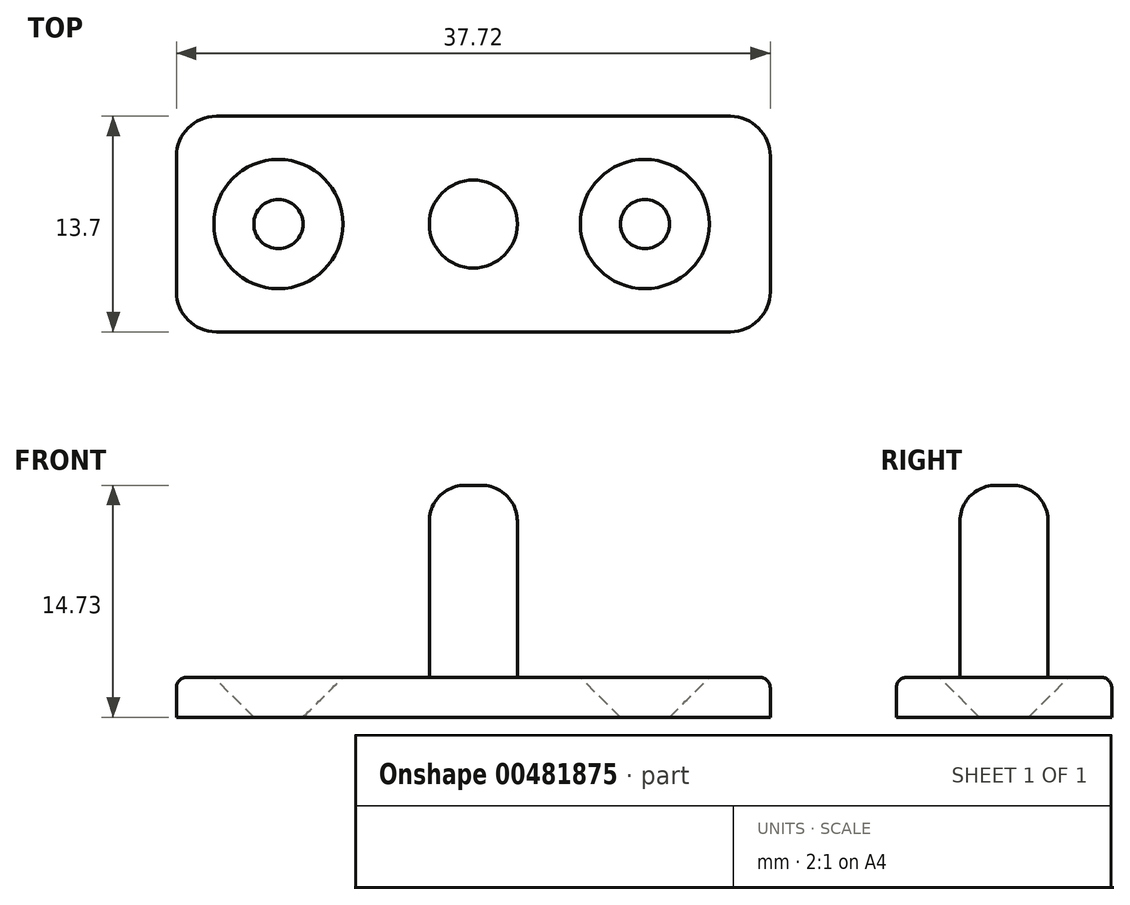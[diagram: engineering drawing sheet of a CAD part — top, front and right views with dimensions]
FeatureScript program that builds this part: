
annotation { "Feature Type Name" : "Feature", "Feature Type Description" : "" }
export const myFeature = defineFeature(function(context is Context, id is Id, definition is map)
    precondition{}
    {
        {
            var Q0;
            Q0=qCreatedBy(makeId("Top.planeOp"),FACE);
            var sketch = newSketch(context, id + "F0", { "sketchPlane" : qUnion([Q0])});
            skLineSegment(sketch, "E0.bottom", {"start": v(18.86, -6.85) * mm, "end": v(-18.86, -6.85) * mm});
            skLineSegment(sketch, "E0.top", {"start": v(18.86, 6.85) * mm, "end": v(-18.86, 6.85) * mm});
            skLineSegment(sketch, "E0.left", {"start": v(18.86, -6.85) * mm, "end": v(18.86, 6.85) * mm});
            skLineSegment(sketch, "E0.right", {"start": v(-18.86, -6.85) * mm, "end": v(-18.86, 6.85) * mm});
            skPoint(sketch, "E0.middle", {"position": v(0, 0) * mm});
            skCircle(sketch, "E1", {"center": v(-12.38, 0) * mm, "radius": 1.56 * mm});
            skCircle(sketch, "E2", {"center": v(10.9, 0) * mm, "radius": 1.56 * mm});
            skCircle(sketch, "E3", {"center": v(0, 0) * mm, "radius": 2.8 * mm});
            skSolve(sketch);
        }
        {
            var Q0;
            Q0=makeQuery(id+"F0.imprint","IMPRINT",FACE,{"disambiguationData":[TD([[makeQuery(id+"F0.imprint","IMPRINT",EDGE,{"derivedFrom":sQuery(id+"F0.wireOp",EDGE,"E3")}),1.0]])]});
            extrude(context, id + "F1", {"entities" : qUnion([Q0]), "depth" : 14.73 * mm});
        }
        {
            var Q0;
            Q0=makeQuery(id+"F0.imprint","IMPRINT",FACE,{"disambiguationData":[TD([[makeQuery(id+"F0.imprint","IMPRINT",EDGE,{"derivedFrom":sQuery(id+"F0.wireOp",EDGE,"E0.bottom")}),-1.0]])]});
            extrude(context, id + "F2", {"entities" : qUnion([Q0]), "operationType" : NewBodyOperationType.ADD, "depth" : 2.54 * mm});
        }
        {
            var Q0;
            Q0=makeQuery(id+"F2.opExtrude","CAP_EDGE",EDGE,{"disambiguationData":[OSD([sQuery(id+"F0.wireOp",EDGE,"E1")])],"isStart":false});
            var Q1;
            Q1=makeQuery(id+"F2.opExtrude","CAP_EDGE",EDGE,{"disambiguationData":[OSD([sQuery(id+"F0.wireOp",EDGE,"E2")])],"isStart":false});
            chamfer(context, id + "F3", {"entities" : qUnion([Q0, Q1]), "width" : 2.54 * mm, "tangentPropagation" : true});
        }
        {
            var Q0;
            Q0=makeQuery(id+"F2.opExtrude","SWEPT_EDGE",EDGE,{"disambiguationData":[OSD([sQuery(id+"F0.wireOp",EDGE,"E0.bottom"),sQuery(id+"F0.wireOp",EDGE,"E0.left")])]});
            var Q1;
            Q1=makeQuery(id+"F2.opExtrude","SWEPT_EDGE",EDGE,{"disambiguationData":[OSD([sQuery(id+"F0.wireOp",EDGE,"E0.top"),sQuery(id+"F0.wireOp",EDGE,"E0.left")])]});
            var Q2;
            Q2=makeQuery(id+"F2.opExtrude","SWEPT_EDGE",EDGE,{"disambiguationData":[OSD([sQuery(id+"F0.wireOp",EDGE,"E0.bottom"),sQuery(id+"F0.wireOp",EDGE,"E0.right")])]});
            var Q3;
            Q3=makeQuery(id+"F2.opExtrude","SWEPT_EDGE",EDGE,{"disambiguationData":[OSD([sQuery(id+"F0.wireOp",EDGE,"E0.top"),sQuery(id+"F0.wireOp",EDGE,"E0.right")])]});
            fillet(context, id + "F4", {"entities" : qUnion([Q0, Q1, Q2, Q3]), "radius" : 2.54 * mm, "tangentPropagation" : true, "allowEdgeOverflow" : false});
        }
        {
            var Q0;
            Q0=makeQuery(id+"F1.opExtrude","CAP_EDGE",EDGE,{"disambiguationData":[OSD([sQuery(id+"F0.wireOp",EDGE,"E3")])],"isStart":false});
            fillet(context, id + "F5", {"entities" : qUnion([Q0]), "radius" : 2.27 * mm, "tangentPropagation" : true, "allowEdgeOverflow" : false});
        }
        {
            var Q0;
            Q0=makeQuery(id+"F2.opExtrude","CAP_EDGE",EDGE,{"disambiguationData":[OSD([sQuery(id+"F0.wireOp",EDGE,"E0.bottom")])],"isStart":false});
            var Q1;
            {var subQ0=sQuery(id+"F0.wireOp",EDGE,"E0.left");var subQ1=sQuery(id+"F0.wireOp",EDGE,"E0.bottom");Q1=makeQuery(id+"F4.opFillet","BLEND_EDGE",EDGE,{"blendedFrom":[makeQuery(id+"F2.opExtrude","SWEPT_EDGE",EDGE,{"disambiguationData":[OSD([subQ1,subQ0])]}),makeQuery(id+"F2.opExtrude","CAP_FACE",FACE,{"disambiguationData":[OSD([subQ1,sQuery(id+"F0.wireOp",EDGE,"E0.top"),subQ0,sQuery(id+"F0.wireOp",EDGE,"E0.right"),sQuery(id+"F0.wireOp",EDGE,"E1"),sQuery(id+"F0.wireOp",EDGE,"E2"),sQuery(id+"F0.wireOp",EDGE,"E3")])],"isStart":false})],"blendedInto":[makeQuery(id+"F2.opExtrude","CAP_FACE",FACE,{"disambiguationData":[OSD([subQ1,sQuery(id+"F0.wireOp",EDGE,"E0.top"),subQ0,sQuery(id+"F0.wireOp",EDGE,"E0.right"),sQuery(id+"F0.wireOp",EDGE,"E1"),sQuery(id+"F0.wireOp",EDGE,"E2"),sQuery(id+"F0.wireOp",EDGE,"E3")])],"isStart":false})]});}
            var Q2;
            Q2=makeQuery(id+"F2.opExtrude","CAP_EDGE",EDGE,{"disambiguationData":[OSD([sQuery(id+"F0.wireOp",EDGE,"E0.left")])],"isStart":false});
            var Q3;
            Q3=makeQuery(id+"F2.opExtrude","CAP_EDGE",EDGE,{"disambiguationData":[OSD([sQuery(id+"F0.wireOp",EDGE,"E0.top")])],"isStart":false});
            var Q4;
            {var subQ0=sQuery(id+"F0.wireOp",EDGE,"E0.left");var subQ1=sQuery(id+"F0.wireOp",EDGE,"E0.top");Q4=makeQuery(id+"F4.opFillet","BLEND_EDGE",EDGE,{"blendedFrom":[makeQuery(id+"F2.opExtrude","SWEPT_EDGE",EDGE,{"disambiguationData":[OSD([subQ1,subQ0])]}),makeQuery(id+"F2.opExtrude","CAP_FACE",FACE,{"disambiguationData":[OSD([sQuery(id+"F0.wireOp",EDGE,"E0.bottom"),subQ1,subQ0,sQuery(id+"F0.wireOp",EDGE,"E0.right"),sQuery(id+"F0.wireOp",EDGE,"E1"),sQuery(id+"F0.wireOp",EDGE,"E2"),sQuery(id+"F0.wireOp",EDGE,"E3")])],"isStart":false})],"blendedInto":[makeQuery(id+"F2.opExtrude","CAP_FACE",FACE,{"disambiguationData":[OSD([sQuery(id+"F0.wireOp",EDGE,"E0.bottom"),subQ1,subQ0,sQuery(id+"F0.wireOp",EDGE,"E0.right"),sQuery(id+"F0.wireOp",EDGE,"E1"),sQuery(id+"F0.wireOp",EDGE,"E2"),sQuery(id+"F0.wireOp",EDGE,"E3")])],"isStart":false})]});}
            var Q5;
            {var subQ0=sQuery(id+"F0.wireOp",EDGE,"E0.right");var subQ1=sQuery(id+"F0.wireOp",EDGE,"E0.top");Q5=makeQuery(id+"F4.opFillet","BLEND_EDGE",EDGE,{"blendedFrom":[makeQuery(id+"F2.opExtrude","SWEPT_EDGE",EDGE,{"disambiguationData":[OSD([subQ1,subQ0])]}),makeQuery(id+"F2.opExtrude","CAP_FACE",FACE,{"disambiguationData":[OSD([sQuery(id+"F0.wireOp",EDGE,"E0.bottom"),subQ1,sQuery(id+"F0.wireOp",EDGE,"E0.left"),subQ0,sQuery(id+"F0.wireOp",EDGE,"E1"),sQuery(id+"F0.wireOp",EDGE,"E2"),sQuery(id+"F0.wireOp",EDGE,"E3")])],"isStart":false})],"blendedInto":[makeQuery(id+"F2.opExtrude","CAP_FACE",FACE,{"disambiguationData":[OSD([sQuery(id+"F0.wireOp",EDGE,"E0.bottom"),subQ1,sQuery(id+"F0.wireOp",EDGE,"E0.left"),subQ0,sQuery(id+"F0.wireOp",EDGE,"E1"),sQuery(id+"F0.wireOp",EDGE,"E2"),sQuery(id+"F0.wireOp",EDGE,"E3")])],"isStart":false})]});}
            var Q6;
            Q6=makeQuery(id+"F2.opExtrude","CAP_EDGE",EDGE,{"disambiguationData":[OSD([sQuery(id+"F0.wireOp",EDGE,"E0.right")])],"isStart":false});
            var Q7;
            {var subQ0=sQuery(id+"F0.wireOp",EDGE,"E0.right");var subQ1=sQuery(id+"F0.wireOp",EDGE,"E0.bottom");Q7=makeQuery(id+"F4.opFillet","BLEND_EDGE",EDGE,{"blendedFrom":[makeQuery(id+"F2.opExtrude","SWEPT_EDGE",EDGE,{"disambiguationData":[OSD([subQ1,subQ0])]}),makeQuery(id+"F2.opExtrude","CAP_FACE",FACE,{"disambiguationData":[OSD([subQ1,sQuery(id+"F0.wireOp",EDGE,"E0.top"),sQuery(id+"F0.wireOp",EDGE,"E0.left"),subQ0,sQuery(id+"F0.wireOp",EDGE,"E1"),sQuery(id+"F0.wireOp",EDGE,"E2"),sQuery(id+"F0.wireOp",EDGE,"E3")])],"isStart":false})],"blendedInto":[makeQuery(id+"F2.opExtrude","CAP_FACE",FACE,{"disambiguationData":[OSD([subQ1,sQuery(id+"F0.wireOp",EDGE,"E0.top"),sQuery(id+"F0.wireOp",EDGE,"E0.left"),subQ0,sQuery(id+"F0.wireOp",EDGE,"E1"),sQuery(id+"F0.wireOp",EDGE,"E2"),sQuery(id+"F0.wireOp",EDGE,"E3")])],"isStart":false})]});}
            fillet(context, id + "F6", {"entities" : qUnion([Q0, Q1, Q2, Q3, Q4, Q5, Q6, Q7]), "radius" : 0.67 * mm, "tangentPropagation" : true, "allowEdgeOverflow" : false});
        }
    });
